# Revit family: PDU básico con amperímetro
name_source: partatom
category: Installations électriques
units: mm (PartAtom-declared; Revit-internal decimal feet)

## family parameters
Basée sur le plan de construction = Non
Conserver l'orientation des annotations = Non
Cote de connecteur circulaire = Utiliser le diamètre
Couper avec des vides une fois chargée = Non
Numéro OmniClass = 23.80.00.00
Partagée = Non
Point de calcul de pièce = Non
Titre OmniClass = Electric Power and Lighting
Toujours verticalement = Oui
Type d'élément = Normal

## types (2) — shared parameters
Clase de aplicación = EC002762
Color = Negro
Conectable con internet box = Non
Dirección de montaje = Vertical
E-catalogo enlace = https://www.legrand.fr
Fabricant = LEGRAND
Formulación BIM = Linkeo DATA CENTER BASIC PDU
Frecuencia eléctrica = 50-50
Función = Unidad DE DISTRIBUTION D'ENERGIE
IP = IP20
Marcaje = Oui
Numero RAL = 9017
Prise_alimentation = Alimentation : Prise rotative
Programación = Non applicable
Tipo de tensión = AC
zero-valued in all types: Elévation par défaut

## per-type parameters (varying)
| type | 646166 | 646170 | Anchura (mm) | Consumo pasivo | Corriente de alimentación | Description | EAN | Longitud | Número de disyuntores | Número de fases | Número de pieza Legrand | Número de tomas C13 | Número de tomas C19 | Profondeur cuve + capot | Profundidad (mm) | Sección de cable MIN_MAX | Tipo de conexión eléctrica |
| PDU 0U LPM 1P 32A 20xC13+4xC19 | Oui | Non | 44 mm | 37 mA | 32-32 | PDU BASIC 0U LPM 1 PHASE 32A , 20+4 C13/C19 LOCKING OUTLETS , IEC 60309 | 3414972471435 | 1227 mm | 2 | 1 | LG-646966 | 20 | 4 | 58 mm | 85 mm | 6-6 | CEE 32 A |
| PDU HD 0U LPM 3P 16A 36xC13+6xC19 | Non | Oui | 52 mm  [stored 0.170604 ft] | 71 mA | 16-16 | PDU HD BASIC 0U LPM 3 PHASE 16A , 36+6 C13/C19  LOCKING OUTLETS , IEC 60309 | 3414972471442 | 1248 mm  [stored 4.09449 ft] | 0 | 3 | LG-646970 | 36 | 6 | 65 mm  [stored 0.213255 ft] | 92 mm | 2.5-2.5 | CEE 16 A |

note: [stored X ft] marks values corroborated as IEEE doubles in the binary element streams (Revit-internal decimal feet)
